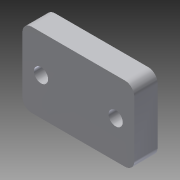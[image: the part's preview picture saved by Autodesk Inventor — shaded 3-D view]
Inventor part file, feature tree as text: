
AUTODESK INVENTOR PART (.ipt)
format: ipt  version: 2014 (Build 180170000, 170)  size: 95,232 bytes
history: native  units: in
note: dims shown in document units (in); Inventor stores cm internally (conversion verified against a paired STEP export)
features: extrude x1, sketch x1
ambient origin geometry x8: Origin, YZ Plane, XZ Plane, XY Plane, X Axis, Y Axis, Z Axis, Center Point
bodies: Solid1 (feature_tree)
feature tree (2):
  extrude  "Extrusion1"  Depth=1.0in
  sketch  "Sketch1"  dims[d0=1.5in d1=1.0in d2=0.19in d3=0.25in d5=0.7874in d7=1.0in d8=0.3937in d10=1.0in d20=0.125in d21=0.3125in d22=0.0in]
